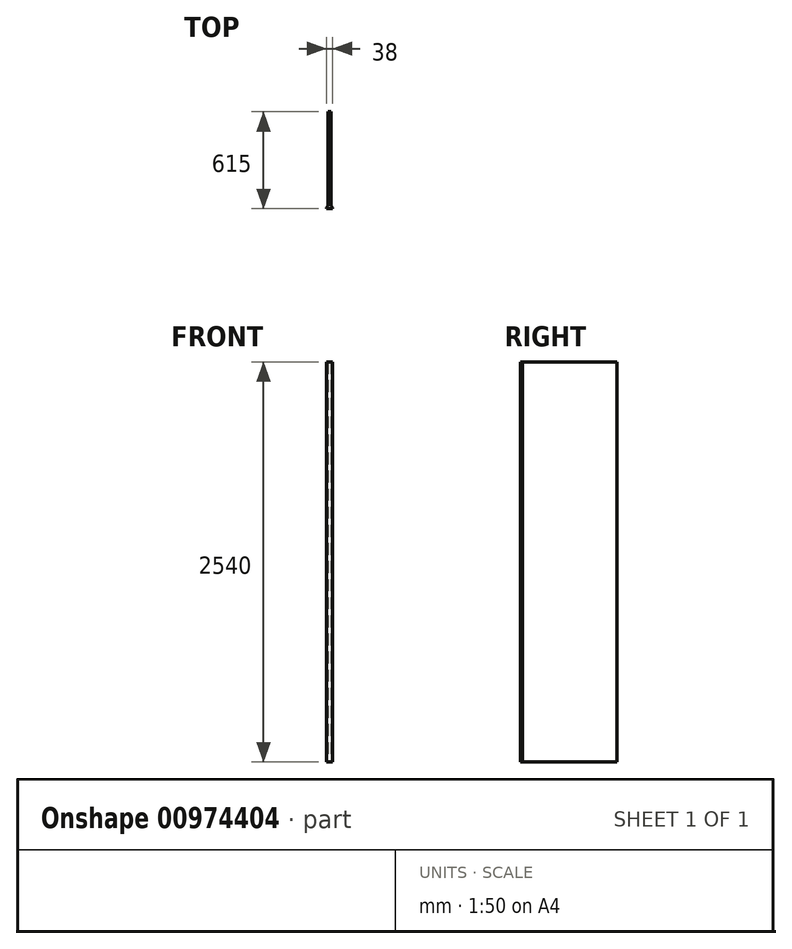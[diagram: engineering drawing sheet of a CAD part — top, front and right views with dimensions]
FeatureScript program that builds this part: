
annotation { "Feature Type Name" : "Feature", "Feature Type Description" : "" }
export const myFeature = defineFeature(function(context is Context, id is Id, definition is map)
    precondition{}
    {
        {
            var Q0;
            Q0=qCreatedBy(makeId("Right.planeOp"),FACE);
            var sketch = newSketch(context, id + "F0", { "sketchPlane" : qUnion([Q0])});
            skLineSegment(sketch, "E0.bottom", {"start": v(300, 1270) * mm, "end": v(-300, 1270) * mm});
            skLineSegment(sketch, "E0.top", {"start": v(300, -1270) * mm, "end": v(-300, -1270) * mm});
            skLineSegment(sketch, "E0.left", {"start": v(300, 1270) * mm, "end": v(300, -1270) * mm});
            skLineSegment(sketch, "E0.right", {"start": v(-300, 1270) * mm, "end": v(-300, -1270) * mm});
            skPoint(sketch, "E0.middle", {"position": v(0, 0) * mm});
            skLineSegment(sketch, "E1", {"start": v(300, 1270) * mm, "end": v(300, 730) * mm});
            skLineSegment(sketch, "E2", {"start": v(300, 730) * mm, "end": v(-300, 730) * mm});
            skSolve(sketch);
        }
        {
            var Q0;
            {var subQ0=sQuery(id+"F0.wireOp",EDGE,"E0.bottom");Q0=makeQuery(id+"F0.imprint","IMPRINT",FACE,{"disambiguationData":[TD([[makeQuery(id+"F0.imprint","IMPRINT",EDGE,{"derivedFrom":subQ0}),1.0]])]});}
            extrude(context, id + "F1", {"entities" : qUnion([Q0]), "depth" : 18 * mm, "offsetDistance" : 25 * mm});
        }
        {
            var Q0;
            {var subQ0=sQuery(id+"F0.wireOp",EDGE,"E0.top");Q0=makeQuery(id+"F0.imprint","IMPRINT",FACE,{"disambiguationData":[TD([[makeQuery(id+"F0.imprint","IMPRINT",EDGE,{"derivedFrom":subQ0}),-1.0]])]});}
            extrude(context, id + "F2", {"entities" : qUnion([Q0]), "operationType" : NewBodyOperationType.ADD, "depth" : 18 * mm, "offsetDistance" : 25 * mm});
        }
        {
            var Q0;
            Q0=makeQuery(id+"F1.opExtrude","SWEPT_FACE",FACE,{"disambiguationData":[OSD([sQuery(id+"F0.wireOp",EDGE,"E0.bottom")])]});
            var sketch = newSketch(context, id + "F3", { "sketchPlane" : qUnion([Q0])});
            skLineSegment(sketch, "E3", {"start": v(0, -300) * mm, "end": v(-10, -310) * mm});
            skLineSegment(sketch, "E4", {"start": v(-10, -310) * mm, "end": v(-10, -315) * mm});
            skLineSegment(sketch, "E5", {"start": v(-10, -315) * mm, "end": v(28, -315) * mm});
            skLineSegment(sketch, "E6", {"start": v(28, -315) * mm, "end": v(28, -310) * mm});
            skLineSegment(sketch, "E7", {"start": v(28, -310) * mm, "end": v(18, -300) * mm});
            skSolve(sketch);
        }
        {
            var Q0;
            Q0=makeQuery(id+"F3.imprint","IMPRINT",FACE,{"disambiguationData":[TD([[makeQuery(id+"F3.imprint","IMPRINT",EDGE,{"derivedFrom":sQuery(id+"F3.wireOp",EDGE,"E3")}),1.0]])]});
            extrude(context, id + "F4", {"entities" : qUnion([Q0]), "operationType" : NewBodyOperationType.ADD, "oppositeDirection" : true, "depth" : 2540 * mm, "offsetDistance" : 25 * mm});
        }
    });
